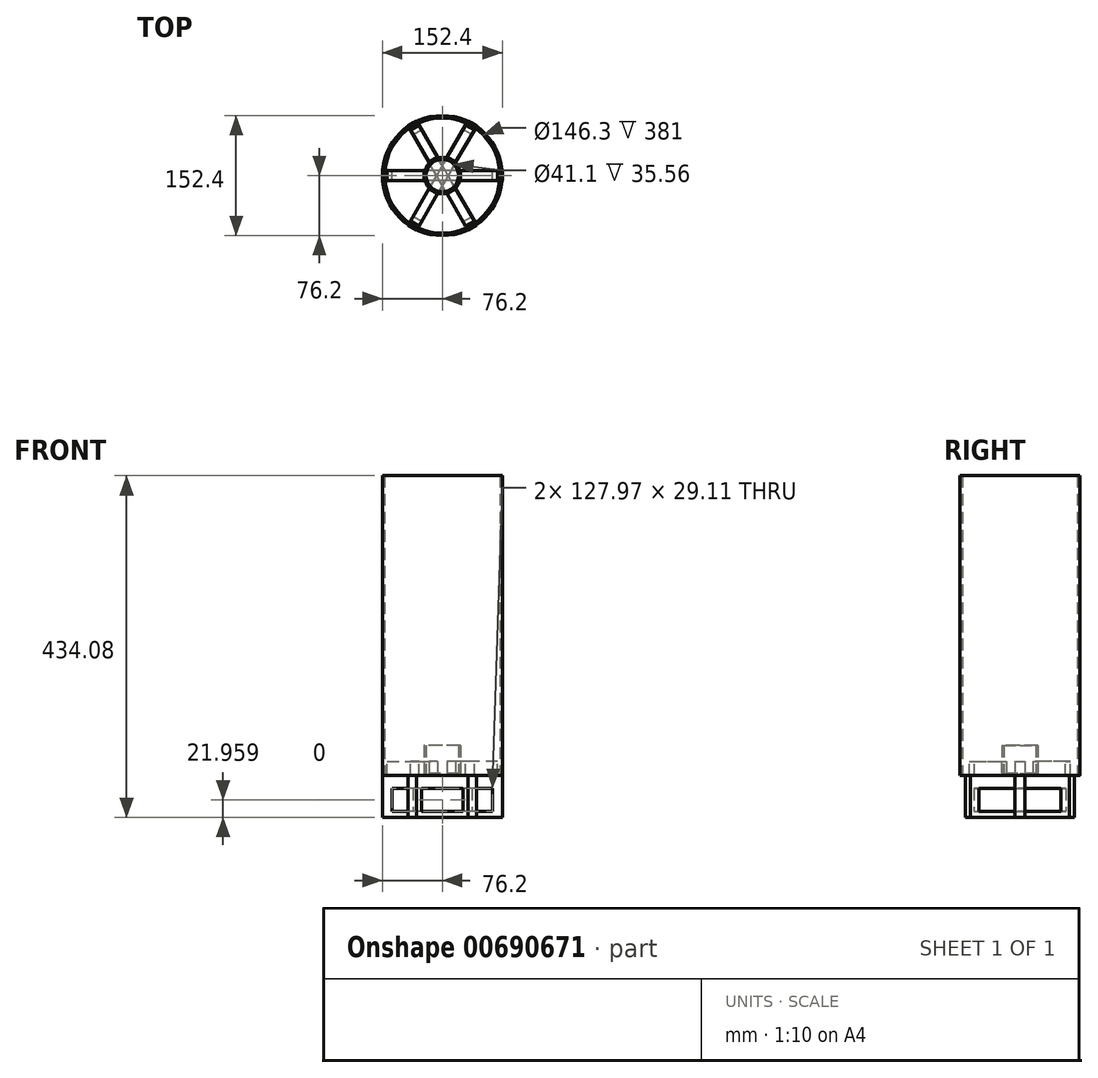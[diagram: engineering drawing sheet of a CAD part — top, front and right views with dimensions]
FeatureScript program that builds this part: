
annotation { "Feature Type Name" : "Feature", "Feature Type Description" : "" }
export const myFeature = defineFeature(function(context is Context, id is Id, definition is map)
    precondition{}
    {
        {
            var Q0;
            Q0=qCreatedBy(makeId("Top.planeOp"),FACE);
            var sketch = newSketch(context, id + "F0", { "sketchPlane" : qUnion([Q0])});
            skCircle(sketch, "E0", {"center": v(0, 0) * mm, "radius": 76.2 * mm});
            skCircle(sketch, "E1.0", {"center": v(0, 0) * mm, "radius": 73.15 * mm});
            skCircle(sketch, "E2", {"center": v(0, 0) * mm, "radius": 23.09 * mm});
            skSolve(sketch);
        }
        {
            var Q0;
            Q0 = qSketchRegion(id + "F0", true);
            extrude(context, id + "F1", {"entities" : qUnion([Q0]), "depth" : 381 * mm, "offsetDistance" : 25.4 * mm});
        }
        {
            var Q0;
            Q0=qCreatedBy(makeId("Front.planeOp"),FACE);
            var sketch = newSketch(context, id + "F2", { "sketchPlane" : qUnion([Q0])});
            skLineSegment(sketch, "E3", {"start": v(0, 0) * mm, "end": v(0, 126.2) * mm, "construction": true});
            skLineSegment(sketch, "E4", {"start": v(0, 126.2) * mm, "end": v(0, -104.94) * mm, "construction": true});
            skLineSegment(sketch, "E5", {"start": v(0, -53.08) * mm, "end": v(76.2, -53.08) * mm});
            skLineSegment(sketch, "E6", {"start": v(76.2, -53.08) * mm, "end": v(76.2, 0) * mm});
            skLineSegment(sketch, "E7", {"start": v(76.2, 0) * mm, "end": v(70.28, 0) * mm});
            skLineSegment(sketch, "E8", {"start": v(70.28, 0) * mm, "end": v(70.28, 18.1) * mm});
            skLineSegment(sketch, "E9", {"start": v(70.28, 18.1) * mm, "end": v(23.1, 18.1) * mm});
            skLineSegment(sketch, "E10", {"start": v(23.1, 18.1) * mm, "end": v(23.1, 0) * mm});
            skLineSegment(sketch, "E11", {"start": v(23.1, 0) * mm, "end": v(0, 0) * mm});
            skLineSegment(sketch, "E12.MirrorCS", {"start": v(-76.2, -53.08) * mm, "end": v(-76.2, 0) * mm});
            skLineSegment(sketch, "E13.MirrorCS", {"start": v(-70.28, 18.1) * mm, "end": v(-23.1, 18.1) * mm});
            skLineSegment(sketch, "E14.MirrorCS", {"start": v(0, -53.08) * mm, "end": v(-76.2, -53.08) * mm});
            skLineSegment(sketch, "E15.MirrorCS", {"start": v(-76.2, 0) * mm, "end": v(-70.28, 0) * mm});
            skLineSegment(sketch, "E16.MirrorCS", {"start": v(-23.1, 18.1) * mm, "end": v(-23.1, 0) * mm});
            skLineSegment(sketch, "E17.MirrorCS", {"start": v(-23.1, 0) * mm, "end": v(0, 0) * mm});
            skLineSegment(sketch, "E18.MirrorCS", {"start": v(-70.28, 0) * mm, "end": v(-70.28, 18.1) * mm});
            skLineSegment(sketch, "E19", {"start": v(0, -16.57) * mm, "end": v(63.99, -16.57) * mm});
            skLineSegment(sketch, "E20", {"start": v(63.99, -16.57) * mm, "end": v(63.99, -45.67) * mm});
            skLineSegment(sketch, "E21", {"start": v(63.99, -45.67) * mm, "end": v(0, -45.67) * mm});
            skLineSegment(sketch, "E22.MirrorCS", {"start": v(0, -16.57) * mm, "end": v(-63.99, -16.57) * mm});
            skLineSegment(sketch, "E23.MirrorCS", {"start": v(-63.99, -45.67) * mm, "end": v(0, -45.67) * mm});
            skLineSegment(sketch, "E24.MirrorCS", {"start": v(-63.99, -16.57) * mm, "end": v(-63.99, -45.67) * mm});
            skLineSegment(sketch, "E25.0", {"start": v(-76.2, 0) * mm, "end": v(76.2, 0) * mm});
            skLineSegment(sketch, "E26.0", {"start": v(-23.09, 0) * mm, "end": v(23.09, 0) * mm});
            skSolve(sketch);
        }
        {
            var Q0;
            Q0 = qSketchRegion(id + "F2", true);
            extrude(context, id + "F3", {"entities" : qUnion([Q0]), "endBound" : BoundingType.SYMMETRIC, "depth" : 12.7 * mm, "offsetDistance" : 25.4 * mm});
        }
        {
            var Q0;
            Q0=makeQuery(id+"F3.opExtrude","SWEPT_BODY",BODY,{"disambiguationData":[OSD([sQuery(id+"F2.wireOp",EDGE,"E5"),sQuery(id+"F2.wireOp",EDGE,"E6"),sQuery(id+"F2.wireOp",EDGE,"E7"),sQuery(id+"F2.wireOp",EDGE,"E8"),sQuery(id+"F2.wireOp",EDGE,"E9"),sQuery(id+"F2.wireOp",EDGE,"E10"),sQuery(id+"F2.wireOp",EDGE,"E11"),sQuery(id+"F2.wireOp",EDGE,"E12.MirrorCS"),sQuery(id+"F2.wireOp",EDGE,"E13.MirrorCS"),sQuery(id+"F2.wireOp",EDGE,"E14.MirrorCS"),sQuery(id+"F2.wireOp",EDGE,"E15.MirrorCS"),sQuery(id+"F2.wireOp",EDGE,"E16.MirrorCS"),sQuery(id+"F2.wireOp",EDGE,"E17.MirrorCS"),sQuery(id+"F2.wireOp",EDGE,"E18.MirrorCS"),sQuery(id+"F2.wireOp",EDGE,"E19"),sQuery(id+"F2.wireOp",EDGE,"E20"),sQuery(id+"F2.wireOp",EDGE,"E21"),sQuery(id+"F2.wireOp",EDGE,"E22.MirrorCS"),sQuery(id+"F2.wireOp",EDGE,"E23.MirrorCS"),sQuery(id+"F2.wireOp",EDGE,"E24.MirrorCS")])]});
            var Q1;
            Q1=sQuery(id+"F2.wireOp",EDGE,"E3");
            circularPattern(context, id + "F4", {"entities" : qUnion([Q0]), "axis" : qUnion([Q1]), "angle" : 360 * degree, "instanceCount" : 6, "equalSpace" : true});
        }
        {
            var Q0;
            Q0=qCreatedBy(makeId("Front.planeOp"),FACE);
            var sketch = newSketch(context, id + "F5", { "sketchPlane" : qUnion([Q0])});
            skPoint(sketch, "E27.0", {"position": v(76.2, -53.08) * mm});
            skLineSegment(sketch, "E28.bottom", {"start": v(76.2, -53.08) * mm, "end": v(80.96, -53.08) * mm});
            skLineSegment(sketch, "E28.top", {"start": v(76.2, 361.95) * mm, "end": v(80.96, 361.95) * mm});
            skLineSegment(sketch, "E28.left", {"start": v(76.2, -53.08) * mm, "end": v(76.2, 361.95) * mm});
            skLineSegment(sketch, "E28.right", {"start": v(80.96, -53.08) * mm, "end": v(80.96, 361.95) * mm});
            skLineSegment(sketch, "E29.0", {"start": v(-76.2, 381) * mm, "end": v(76.2, 381) * mm});
            skLineSegment(sketch, "E30", {"start": v(76.2, 381) * mm, "end": v(76.2, 361.95) * mm, "construction": true});
            skSolve(sketch);
        }
        {
            var Q0;
            Q0 = qSketchRegion(id + "F5", true);
            extrude(context, id + "F6", {"entities" : qUnion([Q0]), "endBound" : BoundingType.SYMMETRIC, "depth" : 12.7 * mm, "offsetDistance" : 25.4 * mm});
        }
        {
            var Q0;
            Q0=makeQuery(id+"F6.opExtrude","SWEPT_BODY",BODY,{"disambiguationData":[OSD([sQuery(id+"F5.wireOp",EDGE,"E28.bottom"),sQuery(id+"F5.wireOp",EDGE,"E28.top"),sQuery(id+"F5.wireOp",EDGE,"E28.left"),sQuery(id+"F5.wireOp",EDGE,"E28.right")])]});
            var Q1;
            Q1=sQuery(id+"F2.wireOp",EDGE,"E4");
            circularPattern(context, id + "F7", {"entities" : qUnion([Q0]), "axis" : qUnion([Q1]), "angle" : 360 * degree, "instanceCount" : 2, "equalSpace" : true});
        }
        {
            var Q0;
            Q0=makeQuery(id+"F6.opExtrude","SWEPT_BODY",BODY,{"disambiguationData":[OSD([sQuery(id+"F5.wireOp",EDGE,"E28.bottom"),sQuery(id+"F5.wireOp",EDGE,"E28.top"),sQuery(id+"F5.wireOp",EDGE,"E28.left"),sQuery(id+"F5.wireOp",EDGE,"E28.right")])]});
            var Q1;
            Q1=makeQuery(id+"F7.opPattern","COPY",BODY,{"derivedFrom":makeQuery(id+"F6.opExtrude","SWEPT_BODY",BODY,{"disambiguationData":[OSD([sQuery(id+"F5.wireOp",EDGE,"E28.bottom"),sQuery(id+"F5.wireOp",EDGE,"E28.top"),sQuery(id+"F5.wireOp",EDGE,"E28.left"),sQuery(id+"F5.wireOp",EDGE,"E28.right")])]}),"instanceName":"1"});
            deleteBodies(context, id + "F8", {"entities" : qUnion([Q0, Q1])});
        }
        {
            var Q0;
            Q0=makeQuery(id+"F0.imprint","IMPRINT",FACE,{"disambiguationData":[TD([[makeQuery(id+"F0.imprint","IMPRINT",EDGE,{"derivedFrom":sQuery(id+"F0.wireOp",EDGE,"E2")}),1.0]])]});
            extrude(context, id + "F9", {"entities" : qUnion([Q0]), "depth" : 38.1 * mm, "offsetDistance" : 25.4 * mm});
        }
        {
            var Q0;
            Q0=makeQuery(id+"F9.opExtrude","CAP_FACE",FACE,{"disambiguationData":[OSD([sQuery(id+"F0.wireOp",EDGE,"E2")])],"isStart":false});
            shell(context, id + "F10", {"entities" : qUnion([Q0]), "thickness" : 2.54 * mm});
        }
    });
